# Revit family: BRG-SNT-IOP_ONE PIECE KINGSLEY AD. INT.EF BL-PRATO
name_source: partatom
category: Aparatos sanitarios
units: mm (PartAtom-declared; Revit-internal decimal feet)

## family parameters
Compartido = Sí
Corte con vacíos al cargar = No
Cota de conector redondo = Diámetro de uso
Número OmniClass = 23.45.00.00
Punto de cálculo de habitación = Sí
Se basa en plano de trabajo = No
Siempre vertical = Sí
Tipo de pieza = Normal
Título OmniClass = Sanitary, Laundry, and Cleaning Equipment

## types (1)
- INODORO KINGSLEY ADVANCE ALARGADO
    Conexión AC = Sí
    Conexión AF = Sí
    Conexión de residuos = Sí
    Conexión de ventilación = Sí
    Fabricante = EDESA Ecuador
    Imagen de tipo = <Ninguno>
    Modelo = INODORO KINGSLEY ADVANCE ALARGADO
    URL = https://www.briggs.com.ec
    _ALT_Basamento = 0.4 m
    _ALT_Eje instalación = 0.6 m
    _EDESA_ Alto en cm = 60.3
    _EDESA_ Ancho en cm = 49
    _EDESA_ Categoría = Productos > Sanitarios > Inodoros > One Piece
    _EDESA_ Certificación = Cumple con norma NTE INEN 3082
    _EDESA_ Color = blanco, bone, cotton
    _EDESA_ Conexión hidráulica = Entrada de agua: tubería ø 1/2" Salida de agua: tubería ø 4"
    _EDESA_ Consumo/capacidad de agua en L = 4.1 y 6.0 litros
    _EDESA_ Descripción = Inodoro one piece alargado de tanque bajo, con sistema dual flush superior y asiento slow down. Listo para instalar.
    _EDESA_ Distancia de instalación en cm (muro terminado) = 30.5 cm
    _EDESA_ Garantía = De por vida en funcionamiento y acabado de la cerámica sanitaria
    _EDESA_ Manual de instalación = https://www.briggs.com.ec
    _EDESA_ Marca = BRIGGS
    _EDESA_ Materiales = Cerámica Sanitaria
    _EDESA_ Nombre = INODORO KINGSLEY ADVANCE ALARGADO
    _EDESA_ Peso en kg = 41.3 kg
    _EDESA_ Productos incluídos = Asiento Prato slow down, Herraje dual flush, Botón Dual Flush Square, Set de Anclaje Taza Piso, Sello de Cera, Tapas de Anclaje. Productos Integrados incluye Llave angular para Inodoro con manguera de 12”
    _EDESA_ Productos necesarios para instalación = 0
    _EDESA_ Profundidad en cm = 75.5
    _EDESA_ Sku/código = JSSI6089___1CW
    _EDESA_ Tipo de instalación = Al piso
